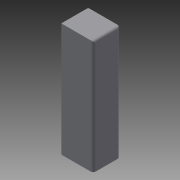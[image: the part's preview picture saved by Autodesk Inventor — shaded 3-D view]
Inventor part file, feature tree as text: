
AUTODESK INVENTOR PART (.ipt)
format: ipt  version: 2015 (Build 190159000, 159)  size: 79,360 bytes
history: native  units: mm
features: extrude x1, fillet x1, sketch x1
ambient origin geometry x8: Origin, YZ Plane, XZ Plane, XY Plane, X Axis, Y Axis, Z Axis, Center Point
bodies: Solid1 (feature_tree)
feature tree (3):
  extrude  "Extrusion1"  Depth=97.0mm
  fillet  "Fillet1"  Radius=23.0mm
  sketch  "Sketch1"  dims[d0=28.4mm d1=97.0mm d2=23.0mm d3=0.0mm d4=2.0mm]
